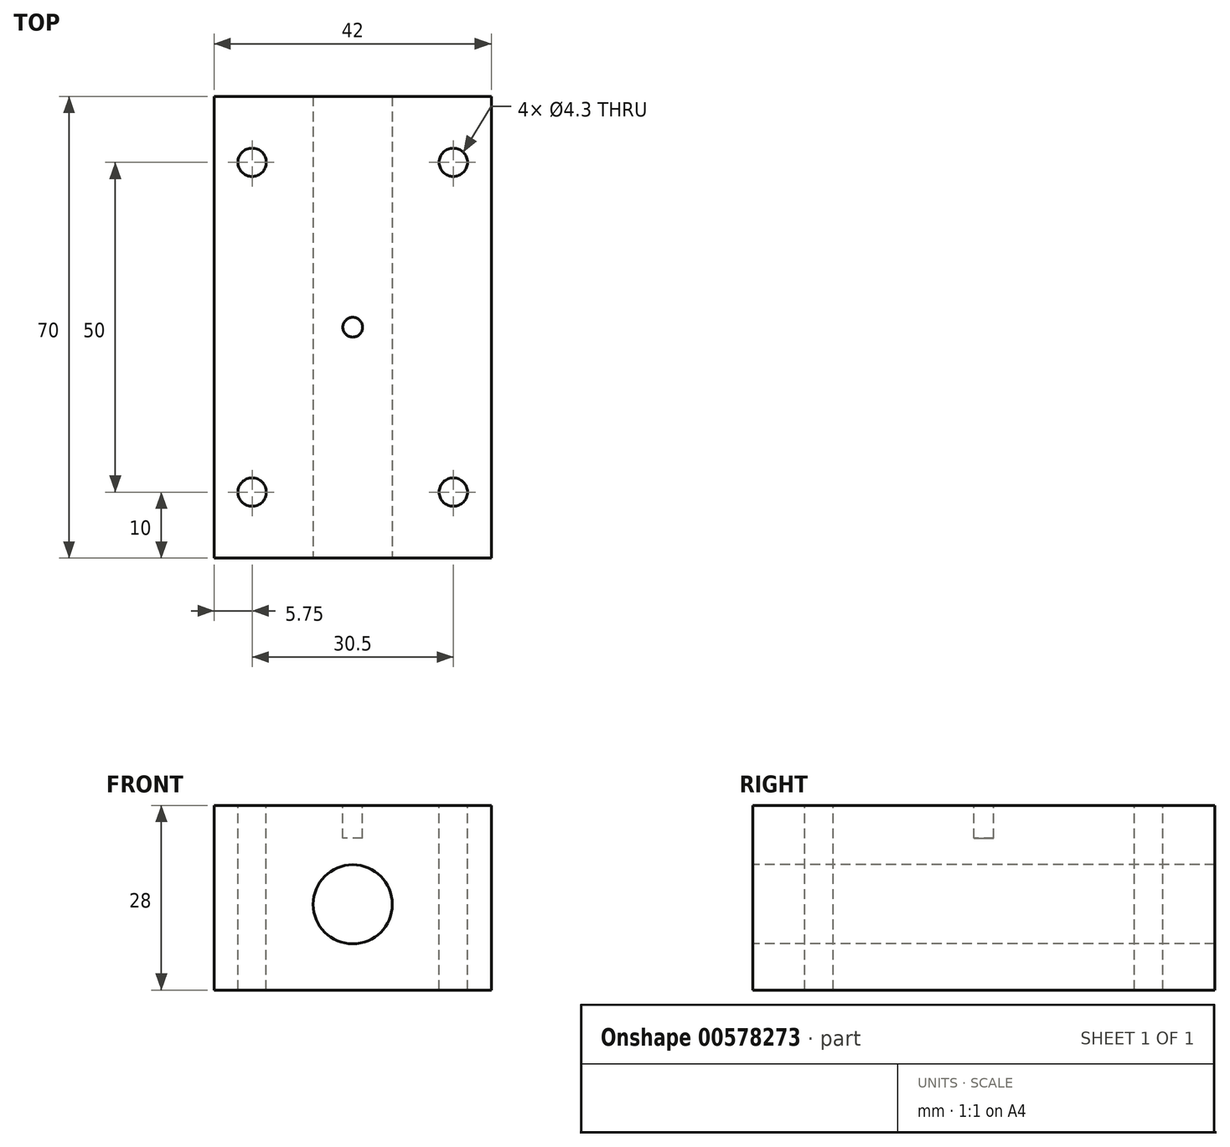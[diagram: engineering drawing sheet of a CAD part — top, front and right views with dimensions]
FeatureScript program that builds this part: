
annotation { "Feature Type Name" : "Feature", "Feature Type Description" : "" }
export const myFeature = defineFeature(function(context is Context, id is Id, definition is map)
    precondition{}
    {
        {
            var Q0;
            Q0=qCreatedBy(makeId("Top.planeOp"),FACE);
            var sketch = newSketch(context, id + "F0", { "sketchPlane" : qUnion([Q0])});
            skLineSegment(sketch, "E0.bottom", {"start": v(-21, 35) * mm, "end": v(21, 35) * mm});
            skLineSegment(sketch, "E0.top", {"start": v(-21, -35) * mm, "end": v(21, -35) * mm});
            skLineSegment(sketch, "E0.left", {"start": v(-21, 35) * mm, "end": v(-21, -35) * mm});
            skLineSegment(sketch, "E0.right", {"start": v(21, 35) * mm, "end": v(21, -35) * mm});
            skPoint(sketch, "E0.middle", {"position": v(0, 0) * mm});
            skCircle(sketch, "E1", {"center": v(-15.25, 25) * mm, "radius": 2.15 * mm});
            skCircle(sketch, "E2.MirrorC", {"center": v(15.25, 25) * mm, "radius": 2.15 * mm});
            skCircle(sketch, "E3.MirrorC", {"center": v(-15.25, -25) * mm, "radius": 2.15 * mm});
            skCircle(sketch, "E4.MirrorC", {"center": v(15.25, -25) * mm, "radius": 2.15 * mm});
            skSolve(sketch);
        }
        {
            var Q0;
            Q0=qSketchRegion(id+"F0",true);
            extrude(context, id + "F1", {"entities" : qUnion([Q0]), "oppositeDirection" : true, "depth" : 28 * mm, "offsetDistance" : 25 * mm});
        }
        {
            var Q0;
            Q0=makeQuery(id+"F1.opExtrude","SWEPT_FACE",FACE,{"disambiguationData":[OSD([sQuery(id+"F0.wireOp",EDGE,"E0.top")])]});
            var sketch = newSketch(context, id + "F2", { "sketchPlane" : qUnion([Q0])});
            skCircle(sketch, "E5", {"center": v(0, -15) * mm, "radius": 6 * mm});
            skSolve(sketch);
        }
        {
            var Q0;
            Q0=qSketchRegion(id+"F2",true);
            extrude(context, id + "F3", {"entities" : qUnion([Q0]), "operationType" : NewBodyOperationType.REMOVE, "oppositeDirection" : true, "depth" : 70 * mm, "offsetDistance" : 25 * mm});
        }
        {
            var Q0;
            Q0=makeQuery(id+"F1.opExtrude","CAP_FACE",FACE,{"disambiguationData":[OSD([sQuery(id+"F0.wireOp",EDGE,"E0.bottom"),sQuery(id+"F0.wireOp",EDGE,"E0.top"),sQuery(id+"F0.wireOp",EDGE,"E0.left"),sQuery(id+"F0.wireOp",EDGE,"E0.right"),sQuery(id+"F0.wireOp",EDGE,"E1"),sQuery(id+"F0.wireOp",EDGE,"E2.MirrorC"),sQuery(id+"F0.wireOp",EDGE,"E3.MirrorC"),sQuery(id+"F0.wireOp",EDGE,"E4.MirrorC")])],"isStart":true});
            var sketch = newSketch(context, id + "F4", { "sketchPlane" : qUnion([Q0])});
            skCircle(sketch, "E6", {"center": v(0, 0) * mm, "radius": 1.5 * mm});
            skSolve(sketch);
        }
        {
            var Q0;
            Q0=qSketchRegion(id+"F4",true);
            extrude(context, id + "F5", {"entities" : qUnion([Q0]), "operationType" : NewBodyOperationType.REMOVE, "oppositeDirection" : true, "depth" : 5 * mm, "offsetDistance" : 25 * mm});
        }
    });
